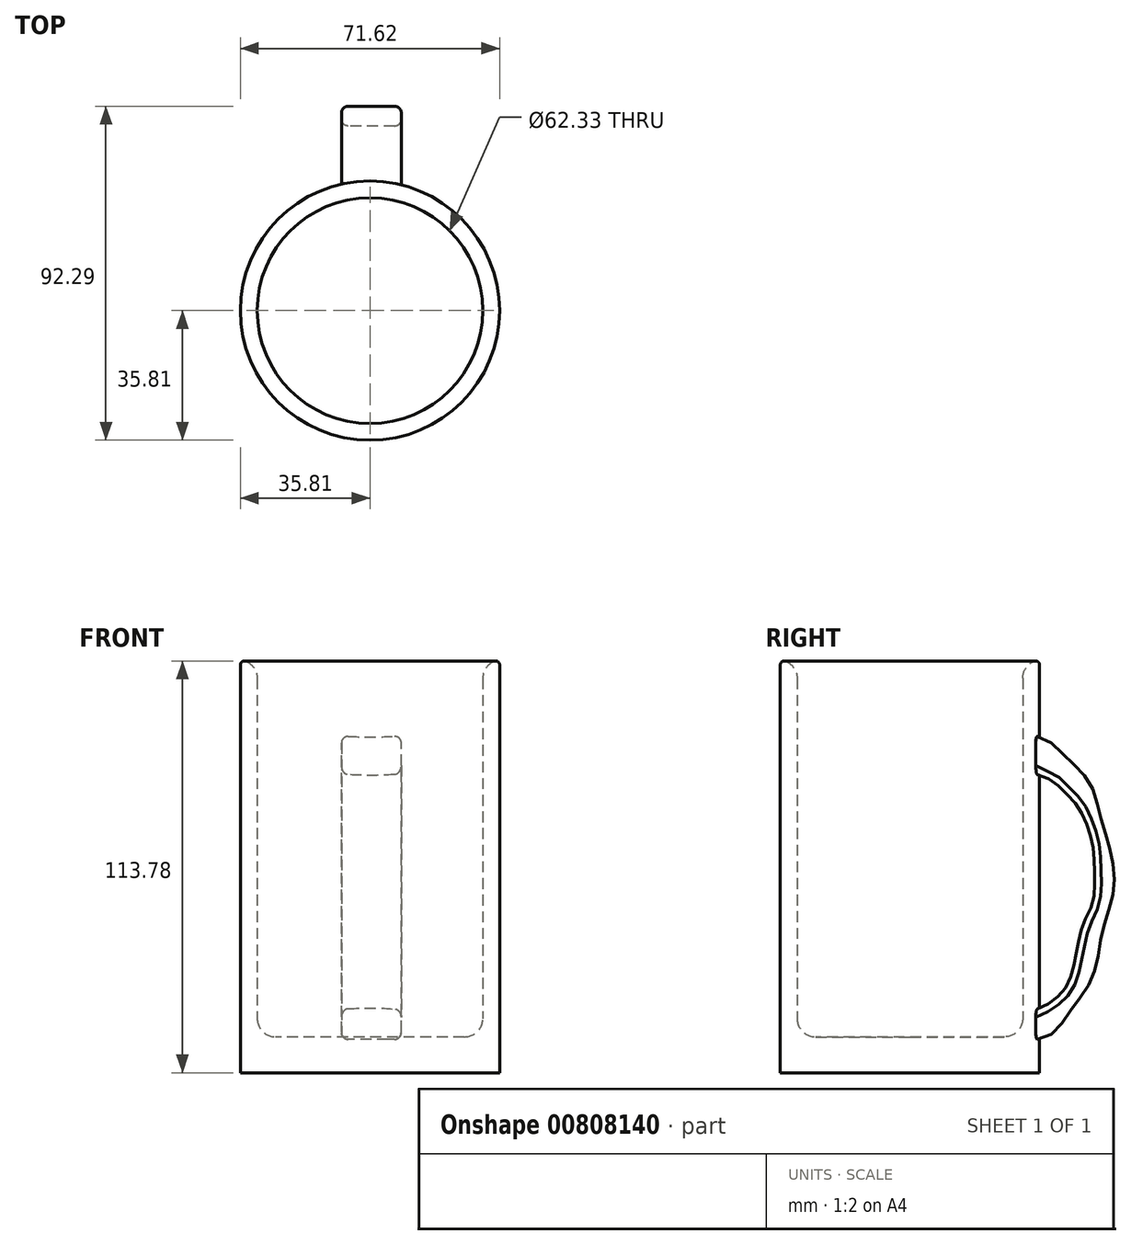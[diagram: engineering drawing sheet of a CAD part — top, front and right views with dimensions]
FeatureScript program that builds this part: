
annotation { "Feature Type Name" : "Feature", "Feature Type Description" : "" }
export const myFeature = defineFeature(function(context is Context, id is Id, definition is map)
    precondition{}
    {
        {
            var Q0;
            Q0=qCreatedBy(makeId("Top.planeOp"),FACE);
            var sketch = newSketch(context, id + "F0", { "sketchPlane" : qUnion([Q0])});
            skCircle(sketch, "E0", {"center": v(0, 0) * mm, "radius": 35.8 * mm});
            skSolve(sketch);
        }
        {
            var Q0;
            Q0=makeQuery(id+"F0.imprint","IMPRINT",FACE,{"disambiguationData":[TD([[makeQuery(id+"F0.imprint","IMPRINT",EDGE,{"derivedFrom":sQuery(id+"F0.wireOp",EDGE,"E0")}),1.0]])]});
            extrude(context, id + "F1", {"entities" : qUnion([Q0]), "oppositeDirection" : true, "depth" : 58.17 * mm, "offsetDistance" : 25.4 * mm});
        }
        {
            var Q0;
            Q0 = qSketchRegion(id + "F0", true);
            extrude(context, id + "F2", {"entities" : qUnion([Q0]), "operationType" : NewBodyOperationType.ADD, "depth" : 55.88 * mm, "offsetDistance" : 25.4 * mm});
        }
        {
            var Q0;
            Q0=qCreatedBy(makeId("Right.planeOp"),FACE);
            var sketch = newSketch(context, id + "F3", { "sketchPlane" : qUnion([Q0])});
            skFitSpline(sketch, "E1", {"points": [v(33.23, 34.44) * mm, v(38.55, 33.37) * mm, v(42.2, 30) * mm, v(49.3, 22.5) * mm, v(52.25, 14.01) * mm, v(56.04, 0) * mm, v(55.95, -9.46) * mm, v(53.23, -18.97) * mm, v(50.35, -31.9) * mm, v(44.77, -40.5) * mm, v(39.73, -47) * mm, v(34.06, -48.6) * mm, v(32.29, -42.93) * mm, v(37.17, -39.65) * mm, v(43.36, -34.07) * mm, v(45.91, -25.32) * mm, v(48.26, -16.19) * mm, v(50.66, -10.47) * mm, v(50.94, -2.31) * mm, v(50.47, 4.7) * mm, v(46.55, 15.08) * mm, v(42.32, 19.77) * mm, v(39.25, 22.57) * mm, v(34.49, 24.6) * mm, v(32.17, 27.98) * mm, v(33.23, 34.44) * mm]});
            skSolve(sketch);
        }
        {
            var Q0;
            Q0 = qSketchRegion(id + "F3", true);
            extrude(context, id + "F4", {"entities" : qUnion([Q0]), "operationType" : NewBodyOperationType.ADD, "depth" : 8.64 * mm, "offsetDistance" : 25.4 * mm});
        }
        {
            var Q0;
            Q0 = qSketchRegion(id + "F3", true);
            extrude(context, id + "F5", {"entities" : qUnion([Q0]), "operationType" : NewBodyOperationType.ADD, "oppositeDirection" : true, "depth" : 7.87 * mm, "offsetDistance" : 25.4 * mm});
        }
        {
            var Q0;
            Q0=makeQuery(id+"F5.boolean.opBoolean","SPLIT",EDGE,{"disambiguationData":[OD(0.0)],"derivedFrom":makeQuery(id+"F5.opExtrude","CAP_EDGE",EDGE,{"disambiguationData":[OSD([sQuery(id+"F3.wireOp",EDGE,"E1")])],"isStart":false})});
            var Q1;
            Q1=makeQuery(id+"F5.boolean.opBoolean","SPLIT",EDGE,{"disambiguationData":[OD(1.0)],"derivedFrom":makeQuery(id+"F5.opExtrude","CAP_EDGE",EDGE,{"disambiguationData":[OSD([sQuery(id+"F3.wireOp",EDGE,"E1")])],"isStart":false})});
            fillet(context, id + "F6", {"entities" : qUnion([Q0, Q1]), "radius" : 1.84 * mm, "tangentPropagation" : true, "allowEdgeOverflow" : false});
        }
        {
            var Q0;
            Q0=makeQuery(id+"F4.boolean.opBoolean","SPLIT",EDGE,{"disambiguationData":[OD(0.0)],"derivedFrom":makeQuery(id+"F4.opExtrude","CAP_EDGE",EDGE,{"disambiguationData":[OSD([sQuery(id+"F3.wireOp",EDGE,"E1")])],"isStart":false})});
            var Q1;
            Q1=makeQuery(id+"F4.boolean.opBoolean","SPLIT",EDGE,{"disambiguationData":[OD(1.0)],"derivedFrom":makeQuery(id+"F4.opExtrude","CAP_EDGE",EDGE,{"disambiguationData":[OSD([sQuery(id+"F3.wireOp",EDGE,"E1")])],"isStart":false})});
            fillet(context, id + "F7", {"entities" : qUnion([Q0, Q1]), "radius" : 1.84 * mm, "tangentPropagation" : true, "allowEdgeOverflow" : false});
        }
        {
            var Q0;
            Q0=qCreatedBy(makeId("Top.planeOp"),FACE);
            var sketch = newSketch(context, id + "F8", { "sketchPlane" : qUnion([Q0])});
            skCircle(sketch, "E2", {"center": v(0, 0) * mm, "radius": 31.17 * mm});
            skSolve(sketch);
        }
        {
            var Q0;
            Q0 = qSketchRegion(id + "F8", true);
            extrude(context, id + "F9", {"entities" : qUnion([Q0]), "operationType" : NewBodyOperationType.REMOVE, "depth" : 67.82 * mm, "offsetDistance" : 25.4 * mm});
        }
        {
            var Q0;
            Q0 = qSketchRegion(id + "F8", true);
            extrude(context, id + "F10", {"entities" : qUnion([Q0]), "operationType" : NewBodyOperationType.REMOVE, "oppositeDirection" : true, "depth" : 48.26 * mm, "offsetDistance" : 25.4 * mm});
        }
        {
            var Q0;
            Q0=makeQuery(id+"F9.boolean.opBoolean","INTERSECT",EDGE,{"derivedFrom":[makeQuery(id+"F2.opExtrude","CAP_FACE",FACE,{"disambiguationData":[OSD([sQuery(id+"F0.wireOp",EDGE,"E0")])],"isStart":false}),makeQuery(id+"F9.opExtrude","SWEPT_FACE",FACE,{"disambiguationData":[OSD([sQuery(id+"F8.wireOp",EDGE,"E2")])]})]});
            fillet(context, id + "F11", {"entities" : qUnion([Q0]), "radius" : 5.08 * mm, "tangentPropagation" : true, "allowEdgeOverflow" : false});
        }
        {
            var Q0;
            {var subQ0=sQuery(id+"F0.wireOp",EDGE,"E0");Q0=makeQuery(id+"F11.opFillet","BLEND_EDGE",EDGE,{"blendedFrom":[makeQuery(id+"F9.boolean.opBoolean","INTERSECT",EDGE,{"derivedFrom":[makeQuery(id+"F2.opExtrude","CAP_FACE",FACE,{"disambiguationData":[OSD([subQ0])],"isStart":false}),makeQuery(id+"F9.opExtrude","SWEPT_FACE",FACE,{"disambiguationData":[OSD([sQuery(id+"F8.wireOp",EDGE,"E2")])]})]}),makeQuery(id+"F2.boolean.opBoolean","MERGE",FACE,{"derivedFrom":[makeQuery(id+"F1.opExtrude","SWEPT_FACE",FACE,{"disambiguationData":[OSD([subQ0])]}),makeQuery(id+"F2.opExtrude","SWEPT_FACE",FACE,{"disambiguationData":[OSD([subQ0])]})]})],"blendedInto":[makeQuery(id+"F2.boolean.opBoolean","MERGE",FACE,{"derivedFrom":[makeQuery(id+"F1.opExtrude","SWEPT_FACE",FACE,{"disambiguationData":[OSD([subQ0])]}),makeQuery(id+"F2.opExtrude","SWEPT_FACE",FACE,{"disambiguationData":[OSD([subQ0])]})]})]});}
            fillet(context, id + "F12", {"entities" : qUnion([Q0]), "radius" : 1.06 * mm, "tangentPropagation" : true, "allowEdgeOverflow" : false});
        }
        {
            var Q0;
            Q0=makeQuery(id+"F10.boolean.opBoolean","COPY",EDGE,{"derivedFrom":makeQuery(id+"F10.opExtrude","CAP_EDGE",EDGE,{"disambiguationData":[OSD([sQuery(id+"F8.wireOp",EDGE,"E2")])],"isStart":false})});
            fillet(context, id + "F13", {"entities" : qUnion([Q0]), "radius" : 5.08 * mm, "tangentPropagation" : true, "allowEdgeOverflow" : false});
        }
    });
